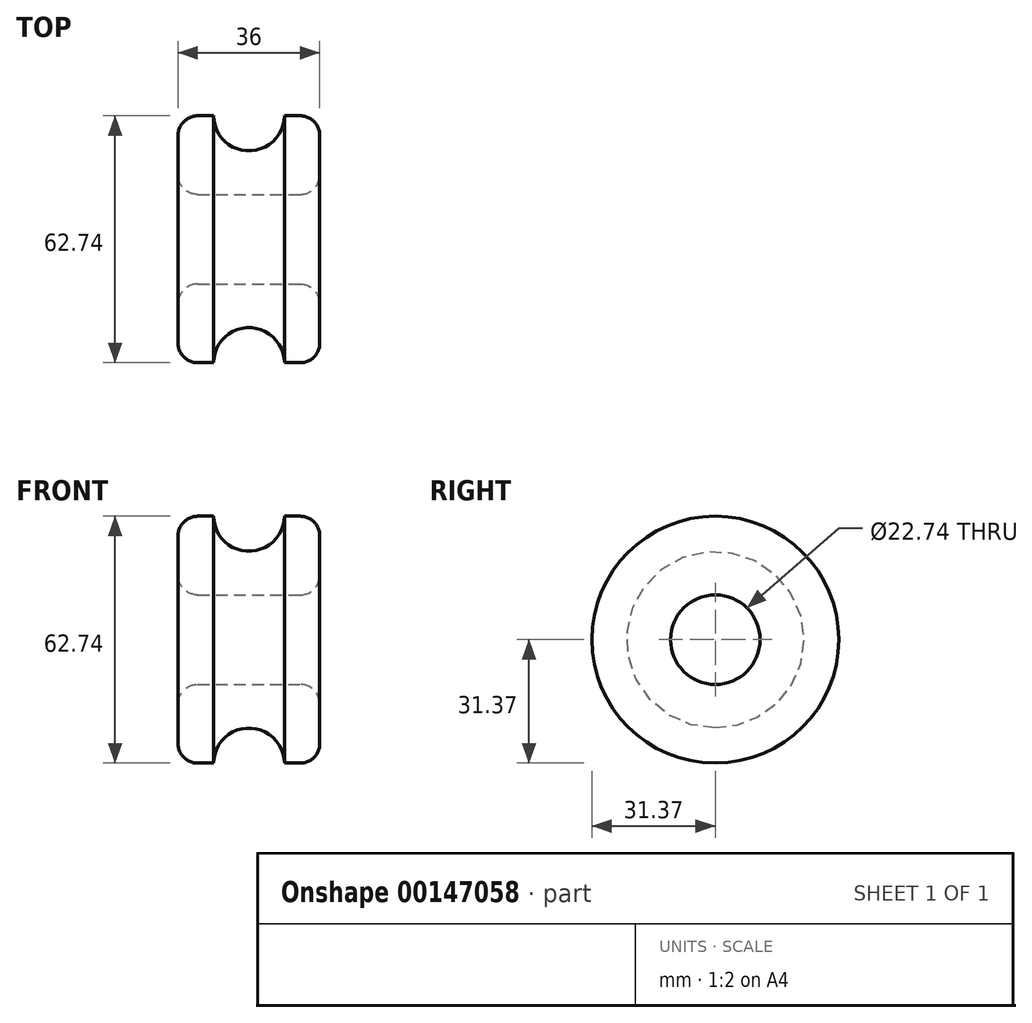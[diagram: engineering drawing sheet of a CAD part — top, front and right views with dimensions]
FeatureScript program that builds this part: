
annotation { "Feature Type Name" : "Feature", "Feature Type Description" : "" }
export const myFeature = defineFeature(function(context is Context, id is Id, definition is map)
    precondition{}
    {
        {
            var Q0;
            Q0=qCreatedBy(makeId("Front.planeOp"),FACE);
            var sketch = newSketch(context, id + "F2", { "sketchPlane" : qUnion([Q0])});
            skLineSegment(sketch, "E0", {"start": v(0, 144.81) * mm, "end": v(0, -127) * mm, "construction": true});
            skLineSegment(sketch, "E1", {"start": v(111.96, 0) * mm, "end": v(-109.88, 0) * mm, "construction": true});
            skArc(sketch, "E2", {"start": v(0, 22.47) * mm, "mid": v(6.33, 25.07) * mm, "end": v(9, 31.37) * mm});
            skLineSegment(sketch, "E3", {"start": v(9, 31.37) * mm, "end": v(13, 31.37) * mm});
            skLineSegment(sketch, "E4", {"start": v(18, 26.37) * mm, "end": v(18, 16.37) * mm});
            skLineSegment(sketch, "E5", {"start": v(13, 11.37) * mm, "end": v(0, 11.37) * mm});
            skLineSegment(sketch, "E6", {"start": v(0, 11.37) * mm, "end": v(0, 22.47) * mm});
            skArc(sketch, "E7", {"start": v(0, 22.97) * mm, "mid": v(8.5, 31.47) * mm, "end": v(0, 39.97) * mm});
            skPoint(sketch, "E8.visualSharp", {"position": v(18, 31.37) * mm});
            skArc(sketch, "E8.filletArc", {"start": v(18, 26.37) * mm, "mid": v(16.53, 29.9) * mm, "end": v(13, 31.37) * mm});
            skPoint(sketch, "E9.visualSharp", {"position": v(18, 11.37) * mm});
            skArc(sketch, "E9.filletArc", {"start": v(13, 11.37) * mm, "mid": v(16.53, 12.83) * mm, "end": v(18, 16.37) * mm});
            skArc(sketch, "E10.MirrorCS", {"start": v(0, 22.47) * mm, "mid": v(-6.33, 25.07) * mm, "end": v(-9, 31.37) * mm});
            skLineSegment(sketch, "E11.MirrorCS", {"start": v(-9, 31.37) * mm, "end": v(-13, 31.37) * mm});
            skArc(sketch, "E12.MirrorCS", {"start": v(-18, 26.37) * mm, "mid": v(-16.53, 29.9) * mm, "end": v(-13, 31.37) * mm});
            skLineSegment(sketch, "E13.MirrorCS", {"start": v(-18, 26.37) * mm, "end": v(-18, 16.37) * mm});
            skArc(sketch, "E14.MirrorCS", {"start": v(-13, 11.37) * mm, "mid": v(-16.53, 12.83) * mm, "end": v(-18, 16.37) * mm});
            skLineSegment(sketch, "E15.MirrorCS", {"start": v(-13, 11.37) * mm, "end": v(0, 11.37) * mm});
            skSolve(sketch);
        }
        {
            var Q0;
            Q0=makeQuery(id+"F2.imprint","IMPRINT",FACE,{"disambiguationData":[TD([[makeQuery(id+"F2.imprint","IMPRINT",EDGE,{"derivedFrom":sQuery(id+"F2.wireOp",EDGE,"E2")}),-1.0]])]});
            var Q1;
            Q1=sQuery(id+"F2.wireOp",EDGE,"E1");
            revolve(context, id + "F3", {"entities" : qUnion([Q0]), "axis" : qUnion([Q1]), "revolveType" : RevolveType.FULL});
        }
        {
            var Q0;
            Q0=makeQuery(id+"F3.opRevolve","SWEPT_BODY",BODY,{"disambiguationData":[OSD([sQuery(id+"F2.wireOp",EDGE,"E2"),sQuery(id+"F2.wireOp",EDGE,"E3"),sQuery(id+"F2.wireOp",EDGE,"E4"),sQuery(id+"F2.wireOp",EDGE,"E5"),sQuery(id+"F2.wireOp",EDGE,"E6"),sQuery(id+"F2.wireOp",EDGE,"E8.filletArc"),sQuery(id+"F2.wireOp",EDGE,"E9.filletArc")])]});
            var Q1;
            Q1=qCreatedBy(makeId("Right.planeOp"),FACE);
            mirror(context, id + "F0", {"operationType" : NewBodyOperationType.ADD, "entities" : qUnion([Q0]), "mirrorPlane" : qUnion([Q1])});
        }
        {
            var Q0;
            Q0=sQuery(id+"F2.wireOp",EDGE,"E7");
            var Q1;
            Q1=sQuery(id+"F2.wireOp",EDGE,"E0");
            revolve(context, id + "F1", {"bodyType" : ToolBodyType.SURFACE, "surfaceEntities" : qUnion([Q0]), "axis" : qUnion([Q1]), "revolveType" : RevolveType.FULL});
        }
        {
            var Q0;
            Q0=makeQuery(id+"F1.opRevolve","SWEPT_BODY",BODY,{"disambiguationData":[OSD([sQuery(id+"F2.wireOp",EDGE,"E7")])]});
            var Q1;
            Q1=sQuery(id+"F2.wireOp",EDGE,"E1");
            circularPattern(context, id + "F4", {"entities" : qUnion([Q0]), "axis" : qUnion([Q1]), "angle" : 325 * degree, "instanceCount" : 10, "equalSpace" : true});
        }
    });
